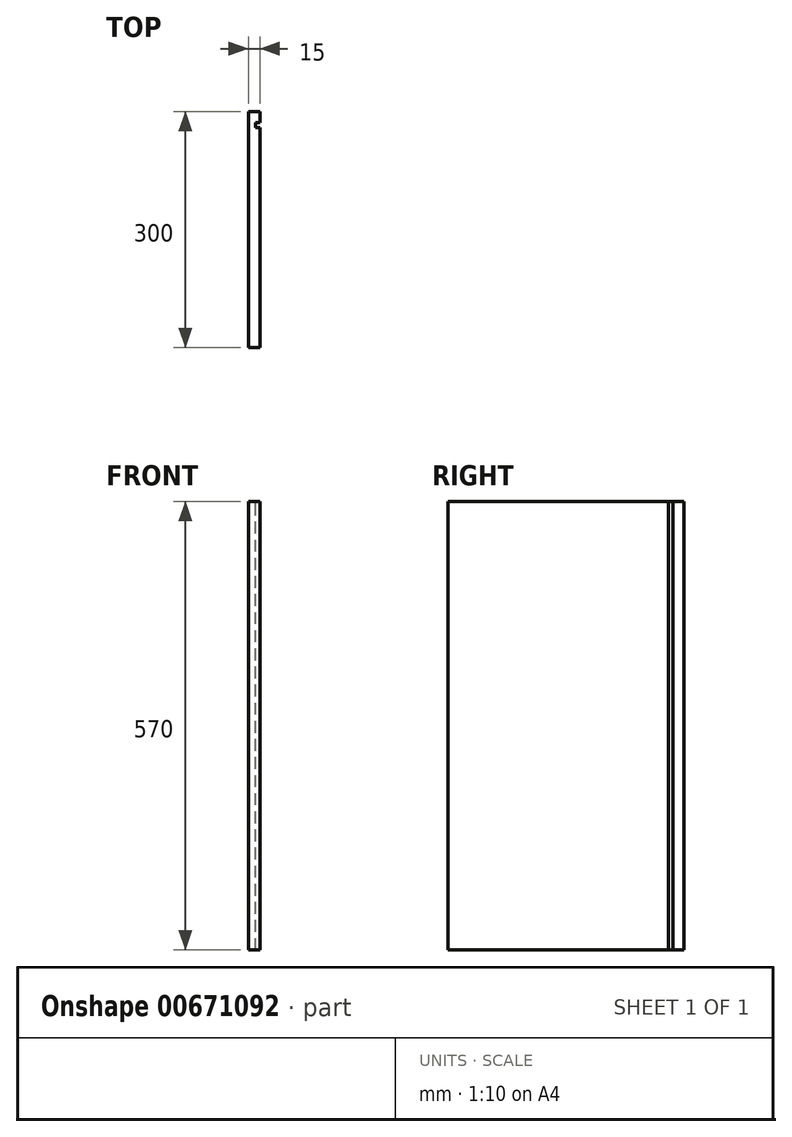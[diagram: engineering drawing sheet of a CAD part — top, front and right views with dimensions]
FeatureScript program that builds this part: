
annotation { "Feature Type Name" : "Feature", "Feature Type Description" : "" }
export const myFeature = defineFeature(function(context is Context, id is Id, definition is map)
    precondition{}
    {
        {
            var Q0;
            Q0=qCreatedBy(makeId("Right.planeOp"),FACE);
            var sketch = newSketch(context, id + "F0", { "sketchPlane" : qUnion([Q0])});
            skLineSegment(sketch, "E0.bottom", {"start": v(0, 0) * mm, "end": v(-300, 0) * mm});
            skLineSegment(sketch, "E0.top", {"start": v(0, 570) * mm, "end": v(-300, 570) * mm});
            skLineSegment(sketch, "E0.left", {"start": v(0, 0) * mm, "end": v(0, 570) * mm});
            skLineSegment(sketch, "E0.right", {"start": v(-300, 0) * mm, "end": v(-300, 570) * mm});
            skSolve(sketch);
        }
        {
            var Q0;
            Q0=makeQuery(id+"F0.imprint","IMPRINT",FACE,{"disambiguationData":[TD([[makeQuery(id+"F0.imprint","IMPRINT",EDGE,{"derivedFrom":sQuery(id+"F0.wireOp",EDGE,"E0.bottom")}),-1.0]])]});
            extrude(context, id + "F1", {"entities" : qUnion([Q0]), "depth" : 15 * mm, "offsetDistance" : 25 * mm});
        }
        {
            var Q0;
            Q0=makeQuery(id+"F1.opExtrude","SWEPT_FACE",FACE,{"disambiguationData":[OSD([sQuery(id+"F0.wireOp",EDGE,"E0.top")])]});
            var sketch = newSketch(context, id + "F2", { "sketchPlane" : qUnion([Q0])});
            skLineSegment(sketch, "E1.bottom", {"start": v(15, -20) * mm, "end": v(9, -20) * mm});
            skLineSegment(sketch, "E1.top", {"start": v(15, -14) * mm, "end": v(9, -14) * mm});
            skLineSegment(sketch, "E1.left", {"start": v(15, -20) * mm, "end": v(15, -14) * mm});
            skLineSegment(sketch, "E1.right", {"start": v(9, -20) * mm, "end": v(9, -14) * mm});
            skSolve(sketch);
        }
        {
            var Q0;
            Q0=makeQuery(id+"F2.imprint","IMPRINT",FACE,{"disambiguationData":[TD([[makeQuery(id+"F2.imprint","IMPRINT",EDGE,{"derivedFrom":sQuery(id+"F2.wireOp",EDGE,"E1.bottom")}),-1.0]])]});
            extrude(context, id + "F3", {"entities" : qUnion([Q0]), "operationType" : NewBodyOperationType.REMOVE, "oppositeDirection" : true, "depth" : 600 * mm, "offsetDistance" : 25 * mm});
        }
    });
